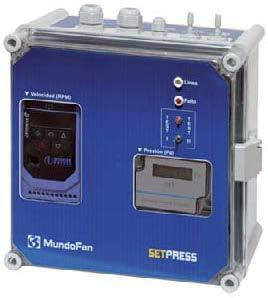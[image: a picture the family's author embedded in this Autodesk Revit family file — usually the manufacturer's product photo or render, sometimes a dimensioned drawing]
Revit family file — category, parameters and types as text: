
# Revit family: SETPRESS-1,5_VE10806
name_source: partatom
category: Aparatos eléctricos
revit_build: Autodesk Revit 2016 (Build: 20150220_1215(x64)
units: mm (PartAtom-declared; Revit-internal decimal feet)

## family parameters
Compartido = No
Corte con vacíos al cargar = No
Cota de conector redondo = Diámetro de uso
Mantener orientación de anotación = No
Número OmniClass = 23.80.00.00
Punto de cálculo de habitación = No
Se basa en plano de trabajo = No
Siempre vertical = Sí
Tipo de pieza = Caja de conexiones
Título OmniClass = Electric Power and Lighting

## types (1)
- SETPRESS
    Alimentación = 230Vac monofásico
    Corriente = 7 A
    Costo = 0 $
    Código de montaje = VE10806
    Descripción = CONTROL EFICIENCIA ENERGETICA PARA VENTILADORES
    Dimensiones máx. = 270x300x170 mm
    Fabricante = SALVADOR ESCODA
    Imagen de tipo = setpress.jpg
    Leds = linea / fallo
    Modelo = SETPRESS 1,5 kW
    Normativas = UNE-EN 12101-6
    Potencia = 1,5 kW
    Regulación = Mediante sonda analógica de presión
    Salida = 230Vac trifásico
    URL = www.salvadorescoda.com
    Visualización = frecuencia (Hz) y presión (Pa)
